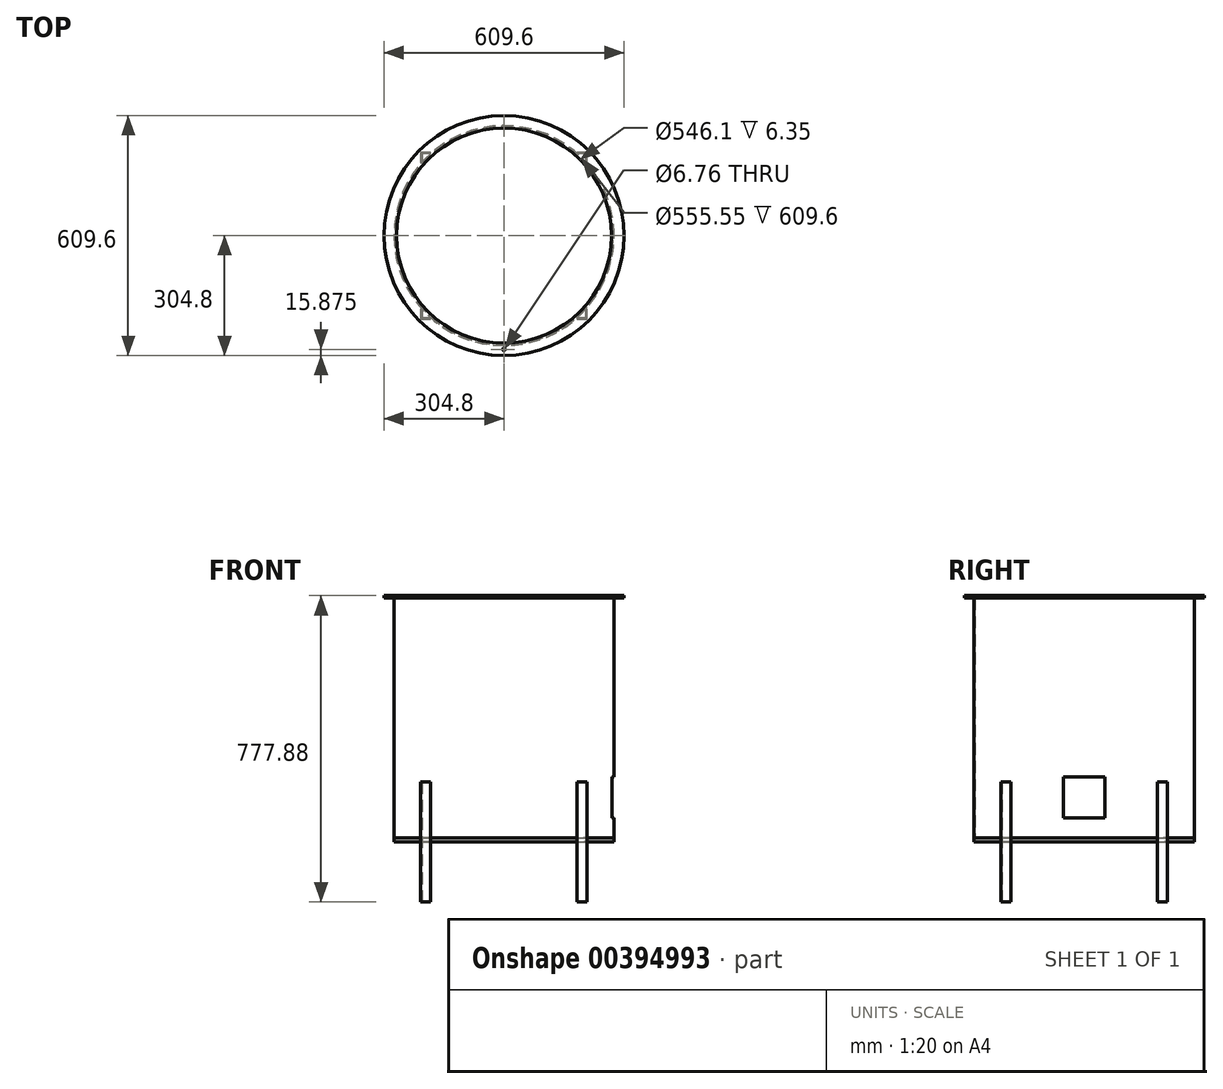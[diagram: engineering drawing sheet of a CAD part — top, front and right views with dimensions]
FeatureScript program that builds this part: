
annotation { "Feature Type Name" : "Feature", "Feature Type Description" : "" }
export const myFeature = defineFeature(function(context is Context, id is Id, definition is map)
    precondition{}
    {
        {
            var Q0;
            Q0=qCreatedBy(makeId("Top.planeOp"),FACE);
            cPlane(context, id + "F0", {"entities" : qUnion([Q0]), "cplaneType" : CPlaneType.OFFSET, "offset" : 152.4 * mm, "width" : 152.4 * mm, "height" : 152.4 * mm});
        }
        {
            var Q0;
            Q0=qCreatedBy(id+"F0.planeOp",FACE);
            var sketch = newSketch(context, id + "F1", { "sketchPlane" : qUnion([Q0])});
            skCircle(sketch, "E0", {"center": v(0, 0) * mm, "radius": 279.4 * mm});
            skSolve(sketch);
        }
        {
            var Q0;
            Q0=makeQuery(id+"F1.imprint","IMPRINT",FACE,{"disambiguationData":[TD([[makeQuery(id+"F1.imprint","IMPRINT",EDGE,{"derivedFrom":sQuery(id+"F1.wireOp",EDGE,"E0")}),1.0]])]});
            extrude(context, id + "F2", {"entities" : qUnion([Q0]), "depth" : 9.52 * mm});
        }
        {
            var Q0;
            Q0=makeQuery(id+"F2.opExtrude","CAP_FACE",FACE,{"disambiguationData":[OSD([sQuery(id+"F1.wireOp",EDGE,"E0")])],"isStart":false});
            cPlane(context, id + "F3", {"entities" : qUnion([Q0]), "cplaneType" : CPlaneType.OFFSET, "offset" : 609.6 * mm, "width" : 152.4 * mm, "height" : 152.4 * mm});
        }
        {
            var Q0;
            Q0=qCreatedBy(id+"F3.planeOp",FACE);
            var sketch = newSketch(context, id + "F4", { "sketchPlane" : qUnion([Q0])});
            skCircle(sketch, "E1.0", {"center": v(0, 0) * mm, "radius": 279.4 * mm, "construction": true});
            skCircle(sketch, "E2", {"center": v(0, 0) * mm, "radius": 304.8 * mm});
            skCircle(sketch, "E3", {"center": v(0, 0) * mm, "radius": 273.05 * mm});
            skLineSegment(sketch, "E4", {"start": v(0, -304.8) * mm, "end": v(0, -273.05) * mm, "construction": true});
            skPoint(sketch, "E5.orphan", {"position": v(0, -399.28) * mm});
            skPoint(sketch, "E6", {"position": v(0, -288.93) * mm});
            skSolve(sketch);
        }
        {
            var Q0;
            Q0=makeQuery(id+"F4.imprint","IMPRINT",FACE,{"disambiguationData":[TD([[makeQuery(id+"F4.imprint","IMPRINT",EDGE,{"derivedFrom":sQuery(id+"F4.wireOp",EDGE,"E2")}),1.0]])]});
            extrude(context, id + "F5", {"entities" : qUnion([Q0]), "depth" : 6.35 * mm});
        }
        {
            var Q0;
            Q0=makeQuery(id+"F2.opExtrude","CAP_FACE",FACE,{"disambiguationData":[OSD([sQuery(id+"F1.wireOp",EDGE,"E0")])],"isStart":false});
            var sketch = newSketch(context, id + "F6", { "sketchPlane" : qUnion([Q0])});
            skCircle(sketch, "E7.0", {"center": v(0, 0) * mm, "radius": 279.4 * mm});
            skCircle(sketch, "E8", {"center": v(0, 0) * mm, "radius": 277.77 * mm});
            skSolve(sketch);
        }
        {
            var Q0;
            Q0=makeQuery(id+"F6.imprint","IMPRINT",FACE,{"disambiguationData":[TD([[makeQuery(id+"F6.imprint","IMPRINT",EDGE,{"derivedFrom":sQuery(id+"F6.wireOp",EDGE,"E7.0")}),1.0]])]});
            var Q1;
            Q1=makeQuery(id+"F5.opExtrude","CAP_FACE",FACE,{"disambiguationData":[OSD([sQuery(id+"F4.wireOp",EDGE,"E1.0"),sQuery(id+"F4.wireOp",EDGE,"E2")])],"isStart":true});
            extrude(context, id + "F7", {"entities" : qUnion([Q0]), "endBound" : BoundingType.UP_TO_SURFACE, "endBoundEntityFace" : qUnion([Q1]), "depth" : 25.4 * mm});
        }
        {
            var Q0;
            Q0=sQuery(id+"F4.wireOp",VERTEX,"E6");
            var Q1;
            Q1=makeQuery(id+"F5.opExtrude","SWEPT_BODY",BODY,{"disambiguationData":[OSD([sQuery(id+"F4.wireOp",EDGE,"E2"),sQuery(id+"F4.wireOp",EDGE,"E3")])]});
            hole(context, id + "F8", {"style" : HoleStyle.SIMPLE, "endStyle" : HoleEndStyle.THROUGH, "oppositeDirection" : true, "standardTappedOrClearance" : lookupTablePath({ "standard" : "ANSI", "fit" : "Normal (ASME)", "size" : "1/4", "type" : "Clearance" }), "standardBlindInLast" : lookupTablePath({ "fit" : "Free", "standard" : "ANSI", "size" : "1/4", "type" : "Clearance" }), "holeDiameter" : 6.76 * mm, "isTappedThrough" : true, "tappedDepth" : 12.7 * mm, "tapClearance" : 3, "locations" : qUnion([Q0]), "scope" : qUnion([Q1])});
        }
        {
            var Q0;
            Q0=qCreatedBy(makeId("Front.planeOp"),FACE);
            var sketch = newSketch(context, id + "F9", { "sketchPlane" : qUnion([Q0])});
            skLineSegment(sketch, "E9", {"start": v(0, 0) * mm, "end": v(0, 935.22) * mm});
            skSolve(sketch);
        }
        {
            var Q0;
            Q0=qCreatedBy(makeId("Top.planeOp"),FACE);
            var sketch = newSketch(context, id + "F10", { "sketchPlane" : qUnion([Q0])});
            skCircle(sketch, "E10.0", {"center": v(0, 0) * mm, "radius": 279.4 * mm, "construction": true});
            skLineSegment(sketch, "E11", {"start": v(0, 0) * mm, "end": v(-263.96, 263.96) * mm, "construction": true});
            skLineSegment(sketch, "E12", {"start": v(-186.14, 208.37) * mm, "end": v(-208.37, 208.37) * mm});
            skLineSegment(sketch, "E13", {"start": v(-208.37, 208.37) * mm, "end": v(-208.37, 186.14) * mm});
            skLineSegment(sketch, "E14", {"start": v(-186.14, 208.37) * mm, "end": v(-186.14, 211.54) * mm});
            skLineSegment(sketch, "E15", {"start": v(-186.14, 211.54) * mm, "end": v(-211.54, 211.54) * mm});
            skLineSegment(sketch, "E16", {"start": v(-211.54, 211.54) * mm, "end": v(-211.54, 186.14) * mm});
            skLineSegment(sketch, "E17", {"start": v(-211.54, 186.14) * mm, "end": v(-208.37, 186.14) * mm});
            skSolve(sketch);
        }
        {
            var Q0;
            Q0=makeQuery(id+"F10.imprint","IMPRINT",FACE,{"disambiguationData":[TD([[makeQuery(id+"F10.imprint","IMPRINT",EDGE,{"derivedFrom":sQuery(id+"F10.wireOp",EDGE,"E12")}),-1.0]])]});
            extrude(context, id + "F11", {"entities" : qUnion([Q0]), "depth" : 304.8 * mm});
        }
        {
            var Q0;
            Q0=makeQuery(id+"F11.opExtrude","SWEPT_BODY",BODY,{"disambiguationData":[OSD([sQuery(id+"F10.wireOp",EDGE,"E12"),sQuery(id+"F10.wireOp",EDGE,"E13"),sQuery(id+"F10.wireOp",EDGE,"E14"),sQuery(id+"F10.wireOp",EDGE,"E15"),sQuery(id+"F10.wireOp",EDGE,"E16"),sQuery(id+"F10.wireOp",EDGE,"E17")])]});
            var Q1;
            Q1=sQuery(id+"F9.wireOp",EDGE,"E9");
            circularPattern(context, id + "F12", {"entities" : qUnion([Q0]), "axis" : qUnion([Q1]), "angle" : 360 * degree, "instanceCount" : 4, "equalSpace" : true});
        }
        {
            var Q0;
            Q0=qCreatedBy(makeId("Right.planeOp"),FACE);
            var sketch = newSketch(context, id + "F13", { "sketchPlane" : qUnion([Q0])});
            skLineSegment(sketch, "E18.0", {"start": v(-279.4, 161.93) * mm, "end": v(279.4, 161.93) * mm, "construction": true});
            skLineSegment(sketch, "E19.bottom", {"start": v(52.39, 212.73) * mm, "end": v(-52.39, 212.73) * mm});
            skLineSegment(sketch, "E19.top", {"start": v(52.39, 317.5) * mm, "end": v(-52.39, 317.5) * mm});
            skLineSegment(sketch, "E19.left", {"start": v(52.39, 212.73) * mm, "end": v(52.39, 317.5) * mm});
            skLineSegment(sketch, "E19.right", {"start": v(-52.39, 212.73) * mm, "end": v(-52.39, 317.5) * mm});
            skPoint(sketch, "E19.middle", {"position": v(0, 265.11) * mm});
            skSolve(sketch);
        }
        {
            var Q0;
            Q0=makeQuery(id+"F13.imprint","IMPRINT",FACE,{"disambiguationData":[TD([[makeQuery(id+"F13.imprint","IMPRINT",EDGE,{"derivedFrom":sQuery(id+"F13.wireOp",EDGE,"E19.bottom")}),-1.0]])]});
            extrude(context, id + "F14", {"entities" : qUnion([Q0]), "operationType" : NewBodyOperationType.REMOVE, "endBound" : BoundingType.THROUGH_ALL, "depth" : 25.4 * mm});
        }
    });
